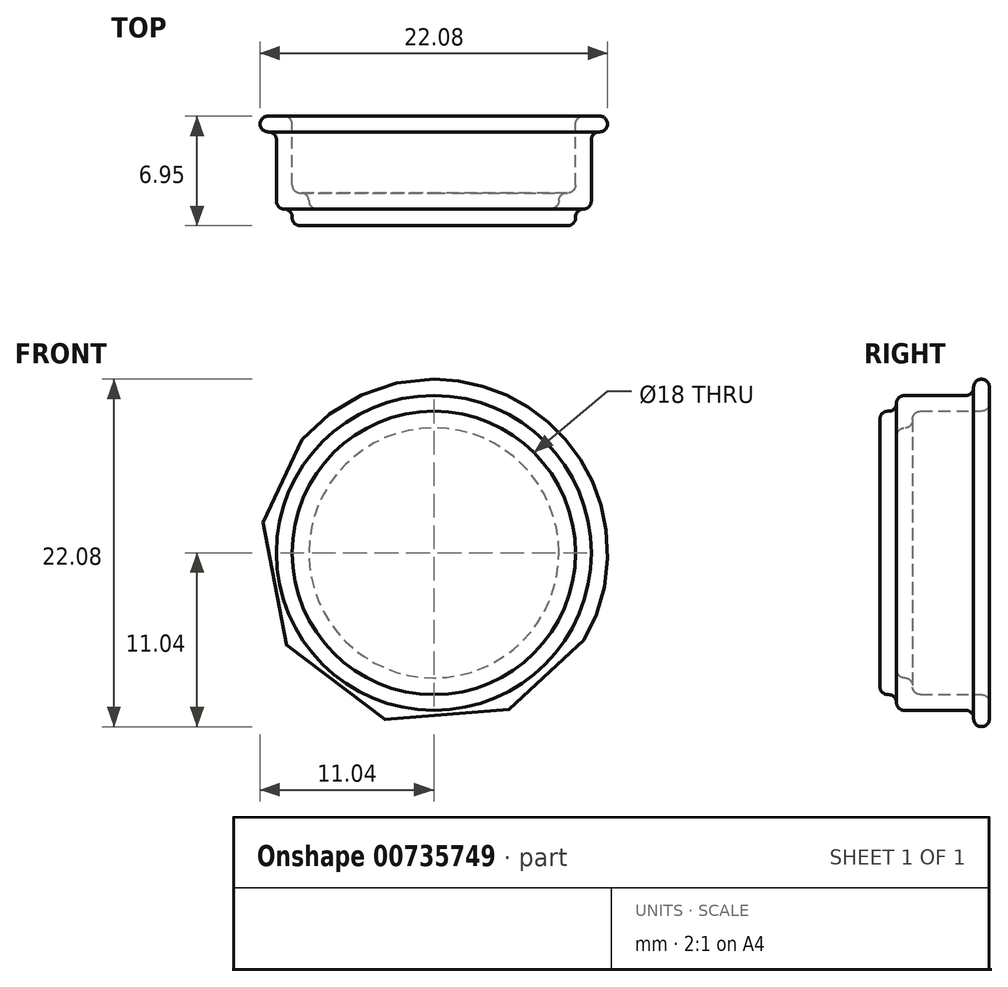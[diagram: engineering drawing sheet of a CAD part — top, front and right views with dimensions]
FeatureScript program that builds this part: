
annotation { "Feature Type Name" : "Feature", "Feature Type Description" : "" }
export const myFeature = defineFeature(function(context is Context, id is Id, definition is map)
    precondition{}
    {
        {
            var Q0;
            Q0=qCreatedBy(makeId("Top.planeOp"),FACE);
            var sketch = newSketch(context, id + "F0", { "sketchPlane" : qUnion([Q0])});
            skLineSegment(sketch, "E0", {"start": v(0, 0) * mm, "end": v(8.5, 0) * mm});
            skLineSegment(sketch, "E1", {"start": v(9, 0.5) * mm, "end": v(9, 0.55) * mm});
            skLineSegment(sketch, "E2", {"start": v(10, 1.55) * mm, "end": v(10, 5.45) * mm});
            skLineSegment(sketch, "E3", {"start": v(10.5, 5.95) * mm, "end": v(10.54, 5.95) * mm});
            skLineSegment(sketch, "E4", {"start": v(10.54, 6.95) * mm, "end": v(9.5, 6.95) * mm});
            skLineSegment(sketch, "E5", {"start": v(9, 6.45) * mm, "end": v(9, 2.58) * mm});
            skLineSegment(sketch, "E6", {"start": v(8.5, 2.08) * mm, "end": v(8.44, 2.08) * mm});
            skLineSegment(sketch, "E7", {"start": v(7.44, 1.08) * mm, "end": v(0, 1.08) * mm});
            skLineSegment(sketch, "E8", {"start": v(0, 1.08) * mm, "end": v(0, 0) * mm});
            skArc(sketch, "E9", {"start": v(8.5, 0) * mm, "mid": v(8.85, 0.15) * mm, "end": v(9, 0.5) * mm});
            skArc(sketch, "E10", {"start": v(9.5, 1.05) * mm, "mid": v(9.15, 0.9) * mm, "end": v(9, 0.55) * mm});
            skPoint(sketch, "E11.orphan", {"position": v(9, 0) * mm});
            skPoint(sketch, "E12.orphan", {"position": v(9, 1.08) * mm});
            skArc(sketch, "E13", {"start": v(9.5, 1.05) * mm, "mid": v(9.85, 1.2) * mm, "end": v(10, 1.55) * mm});
            skArc(sketch, "E14", {"start": v(8.5, 2.08) * mm, "mid": v(8.85, 2.22) * mm, "end": v(9, 2.58) * mm});
            skArc(sketch, "E15", {"start": v(8.44, 2.08) * mm, "mid": v(8.09, 1.93) * mm, "end": v(7.94, 1.58) * mm});
            skArc(sketch, "E16", {"start": v(7.44, 1.08) * mm, "mid": v(7.8, 1.22) * mm, "end": v(7.94, 1.58) * mm});
            skPoint(sketch, "E17.end.orphan", {"position": v(7.94, 1.08) * mm});
            skArc(sketch, "E18", {"start": v(10.5, 5.95) * mm, "mid": v(10.15, 5.8) * mm, "end": v(10, 5.45) * mm});
            skArc(sketch, "E19", {"start": v(9.5, 6.95) * mm, "mid": v(9.15, 6.8) * mm, "end": v(9, 6.45) * mm});
            skArc(sketch, "E20", {"start": v(10.54, 5.95) * mm, "mid": v(11.04, 6.45) * mm, "end": v(10.54, 6.95) * mm});
            skPoint(sketch, "E21.orphan", {"position": v(9, 6.95) * mm});
            skSolve(sketch);
        }
        {
            var Q0;
            Q0 = qSketchRegion(id + "F0", true);
            var Q1;
            Q1=sQuery(id+"F0.wireOp",EDGE,"E8");
            revolve(context, id + "F1", {"surfaceOperationType" : NewSurfaceOperationType.NEW, "entities" : qUnion([Q0]), "axis" : qUnion([Q1]), "revolveType" : RevolveType.FULL});
        }
    });
